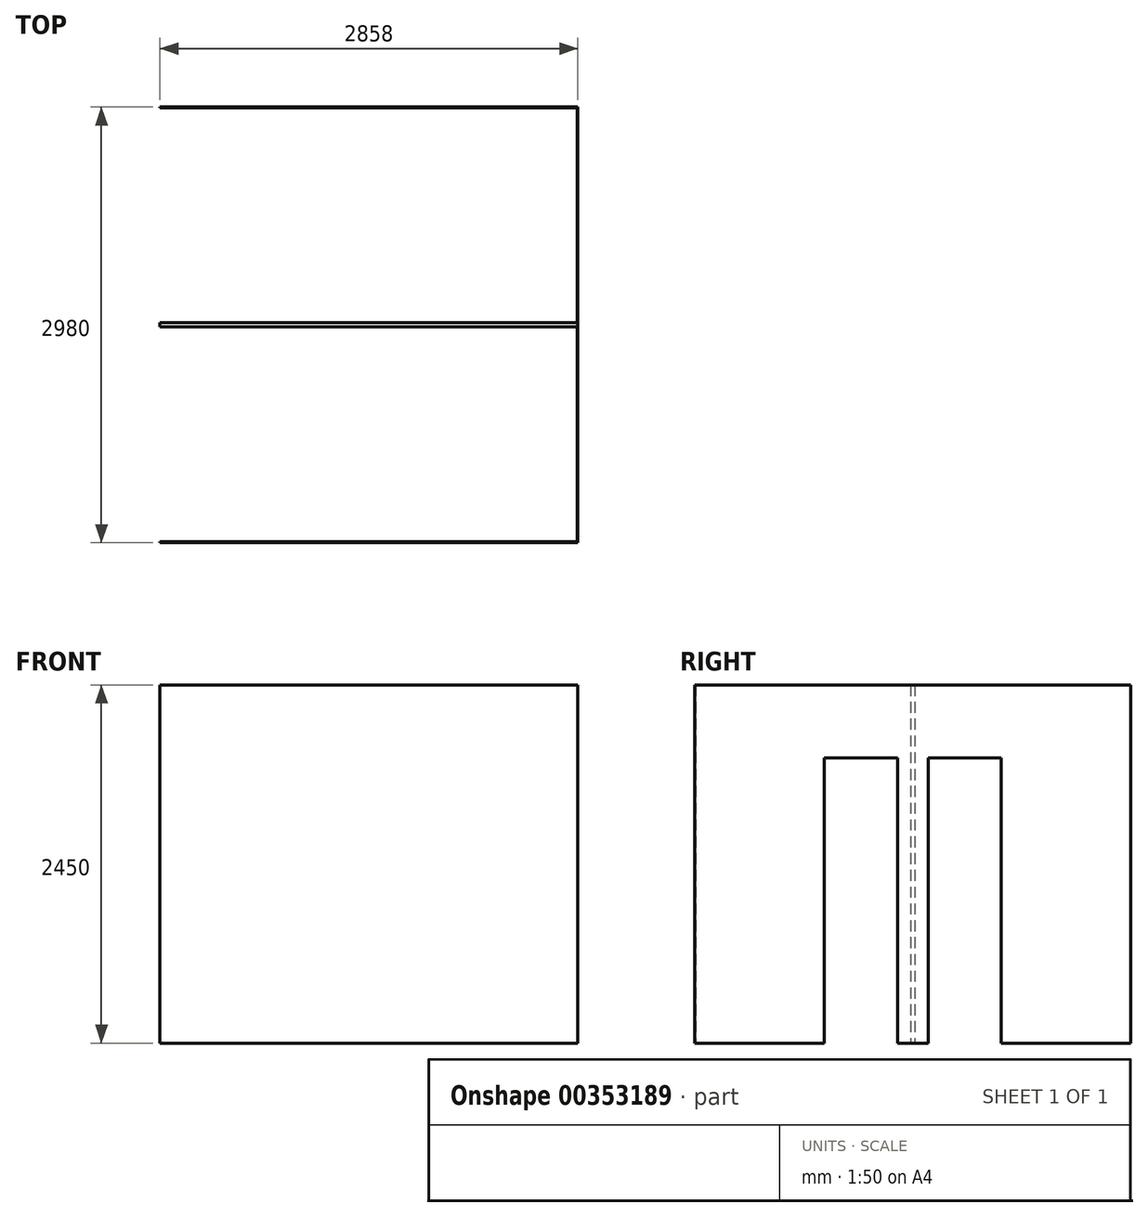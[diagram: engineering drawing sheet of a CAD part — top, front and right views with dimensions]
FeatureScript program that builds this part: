
annotation { "Feature Type Name" : "Feature", "Feature Type Description" : "" }
export const myFeature = defineFeature(function(context is Context, id is Id, definition is map)
    precondition{}
    {
        {
            var Q0;
            Q0=qCreatedBy(makeId("Top.planeOp"),FACE);
            var sketch = newSketch(context, id + "F0", { "sketchPlane" : qUnion([Q0])});
            skLineSegment(sketch, "E0.top", {"start": v(8302.06, 5858.21) * mm, "end": v(5348.06, 5858.21) * mm});
            skLineSegment(sketch, "E1.trimOffspring", {"start": v(8302.06, 8838.21) * mm, "end": v(8302.06, 7358.21) * mm});
            skPoint(sketch, "E2.start.orphan", {"position": v(8302.06, 7348.21) * mm});
            skLineSegment(sketch, "E3.trimOffspring", {"start": v(8302.06, 7338.21) * mm, "end": v(8302.06, 5858.21) * mm});
            skPoint(sketch, "E4.orphan", {"position": v(5348.06, 8858.21) * mm});
            skPoint(sketch, "E5.orphan", {"position": v(5348.06, 8838.21) * mm});
            skLineSegment(sketch, "E6", {"start": v(8302.06, 8838.21) * mm, "end": v(5348.06, 8838.21) * mm});
            skPoint(sketch, "E7.orphan", {"position": v(5348.06, 5858.21) * mm});
            skLineSegment(sketch, "E8.0", {"start": v(8297.06, 8833.21) * mm, "end": v(5348.06, 8833.21) * mm});
            skLineSegment(sketch, "E8.1", {"start": v(8297.06, 8833.21) * mm, "end": v(8297.06, 7363.21) * mm});
            skLineSegment(sketch, "E8.2", {"start": v(8297.06, 7363.21) * mm, "end": v(5343.06, 7363.21) * mm});
            skLineSegment(sketch, "E8.3", {"start": v(8297.06, 5863.21) * mm, "end": v(5348.06, 5863.21) * mm});
            skLineSegment(sketch, "E8.4", {"start": v(8297.06, 7333.21) * mm, "end": v(8297.06, 5863.21) * mm});
            skLineSegment(sketch, "E8.5", {"start": v(8297.06, 7333.21) * mm, "end": v(5343.06, 7333.21) * mm});
            skLineSegment(sketch, "E8.6", {"start": v(5343.06, 7363.21) * mm, "end": v(5343.06, 7333.21) * mm});
            skLineSegment(sketch, "E9", {"start": v(5348.06, 8833.21) * mm, "end": v(5348.06, 8838.21) * mm});
            skLineSegment(sketch, "E10", {"start": v(5348.06, 5863.21) * mm, "end": v(5348.06, 5858.21) * mm});
            skLineSegment(sketch, "E11", {"start": v(8302.06, 7358.21) * mm, "end": v(8302.06, 7338.21) * mm});
            skSolve(sketch);
        }
        {
            var Q0;
            Q0 = qSketchRegion(id + "F0", true);
            extrude(context, id + "F1", {"entities" : qUnion([Q0]), "depth" : 2450 * mm});
        }
        {
            var Q0;
            Q0=makeQuery(id+"F1.opExtrude","SWEPT_FACE",FACE,{"disambiguationData":[OSD([sQuery(id+"F0.wireOp",EDGE,"E8.1")])]});
            var sketch = newSketch(context, id + "F2", { "sketchPlane" : qUnion([Q0])});
            skLineSegment(sketch, "E12.bottom", {"start": v(-7453.21, 1950) * mm, "end": v(-7953.21, 1950) * mm});
            skLineSegment(sketch, "E12.top", {"start": v(-7453.21, 0) * mm, "end": v(-7953.21, 0) * mm});
            skLineSegment(sketch, "E12.left", {"start": v(-7453.21, 1950) * mm, "end": v(-7453.21, 0) * mm});
            skLineSegment(sketch, "E12.right", {"start": v(-7953.21, 1950) * mm, "end": v(-7953.21, 0) * mm});
            skLineSegment(sketch, "E13.0", {"start": v(-7333.21, 2450) * mm, "end": v(-7333.21, 0) * mm});
            skLineSegment(sketch, "E14", {"start": v(-7348.21, 1595.6) * mm, "end": v(-7348.21, 1689.33) * mm});
            skPoint(sketch, "E15.end.orphan", {"position": v(-7453.21, 1595.6) * mm});
            skPoint(sketch, "E16.orphan", {"position": v(-7363.21, 1595.6) * mm});
            skPoint(sketch, "E17.end.orphan", {"position": v(-7333.21, 1595.6) * mm});
            skLineSegment(sketch, "E18.MirrorCS", {"start": v(-7243.21, 1950) * mm, "end": v(-7243.21, 0) * mm});
            skLineSegment(sketch, "E19.MirrorCS", {"start": v(-7243.21, 1950) * mm, "end": v(-6743.21, 1950) * mm});
            skLineSegment(sketch, "E20.MirrorCS", {"start": v(-6743.21, 1950) * mm, "end": v(-6743.21, 0) * mm});
            skLineSegment(sketch, "E21.MirrorCS", {"start": v(-7243.21, 0) * mm, "end": v(-6743.21, 0) * mm});
            skSolve(sketch);
        }
        {
            var Q0;
            Q0 = qSketchRegion(id + "F2", true);
            extrude(context, id + "F3", {"entities" : qUnion([Q0]), "operationType" : NewBodyOperationType.REMOVE, "oppositeDirection" : true, "depth" : 300 * mm});
        }
        {
            var Q0;
            Q0=makeQuery(id+"F1.opExtrude","SWEPT_FACE",FACE,{"disambiguationData":[OSD([sQuery(id+"F0.wireOp",EDGE,"E8.5")])]});
            var sketch = newSketch(context, id + "F4", { "sketchPlane" : qUnion([Q0])});
            skLineSegment(sketch, "E22.left", {"start": v(5343.06, 2450) * mm, "end": v(5343.06, 0) * mm});
            skLineSegment(sketch, "E22.right", {"start": v(5444.06, 2450) * mm, "end": v(5444.06, 0) * mm});
            skLineSegment(sketch, "E23", {"start": v(5444.06, 2450) * mm, "end": v(5343.06, 2450) * mm});
            skLineSegment(sketch, "E24", {"start": v(5444.06, 0) * mm, "end": v(5343.06, 0) * mm});
            skSolve(sketch);
        }
        {
            var Q0;
            Q0 = qSketchRegion(id + "F4", true);
            extrude(context, id + "F5", {"entities" : qUnion([Q0]), "operationType" : NewBodyOperationType.REMOVE, "oppositeDirection" : true, "depth" : 460 * mm});
        }
        {
            var Q0;
            Q0=makeQuery(id+"F1.opExtrude","SWEPT_FACE",FACE,{"disambiguationData":[OSD([sQuery(id+"F0.wireOp",EDGE,"E0.top")])]});
            var sketch = newSketch(context, id + "F6", { "sketchPlane" : qUnion([Q0])});
            skLineSegment(sketch, "E25.0", {"start": v(5444.06, 2450) * mm, "end": v(5444.06, 0) * mm});
            skLineSegment(sketch, "E26", {"start": v(5444.06, 2450) * mm, "end": v(5444.06, 2649.64) * mm});
            skLineSegment(sketch, "E27", {"start": v(5444.06, 2649.64) * mm, "end": v(5038.32, 2649.64) * mm});
            skLineSegment(sketch, "E28", {"start": v(5038.32, 2649.64) * mm, "end": v(5038.32, -210.07) * mm});
            skLineSegment(sketch, "E29", {"start": v(5038.32, -210.07) * mm, "end": v(5444.06, -140.88) * mm});
            skLineSegment(sketch, "E30", {"start": v(5444.06, -140.88) * mm, "end": v(5444.06, 0) * mm});
            skSolve(sketch);
        }
        {
            var Q0;
            Q0 = qSketchRegion(id + "F6", true);
            extrude(context, id + "F7", {"entities" : qUnion([Q0]), "operationType" : NewBodyOperationType.REMOVE, "oppositeDirection" : true, "depth" : 4630 * mm});
        }
    });
